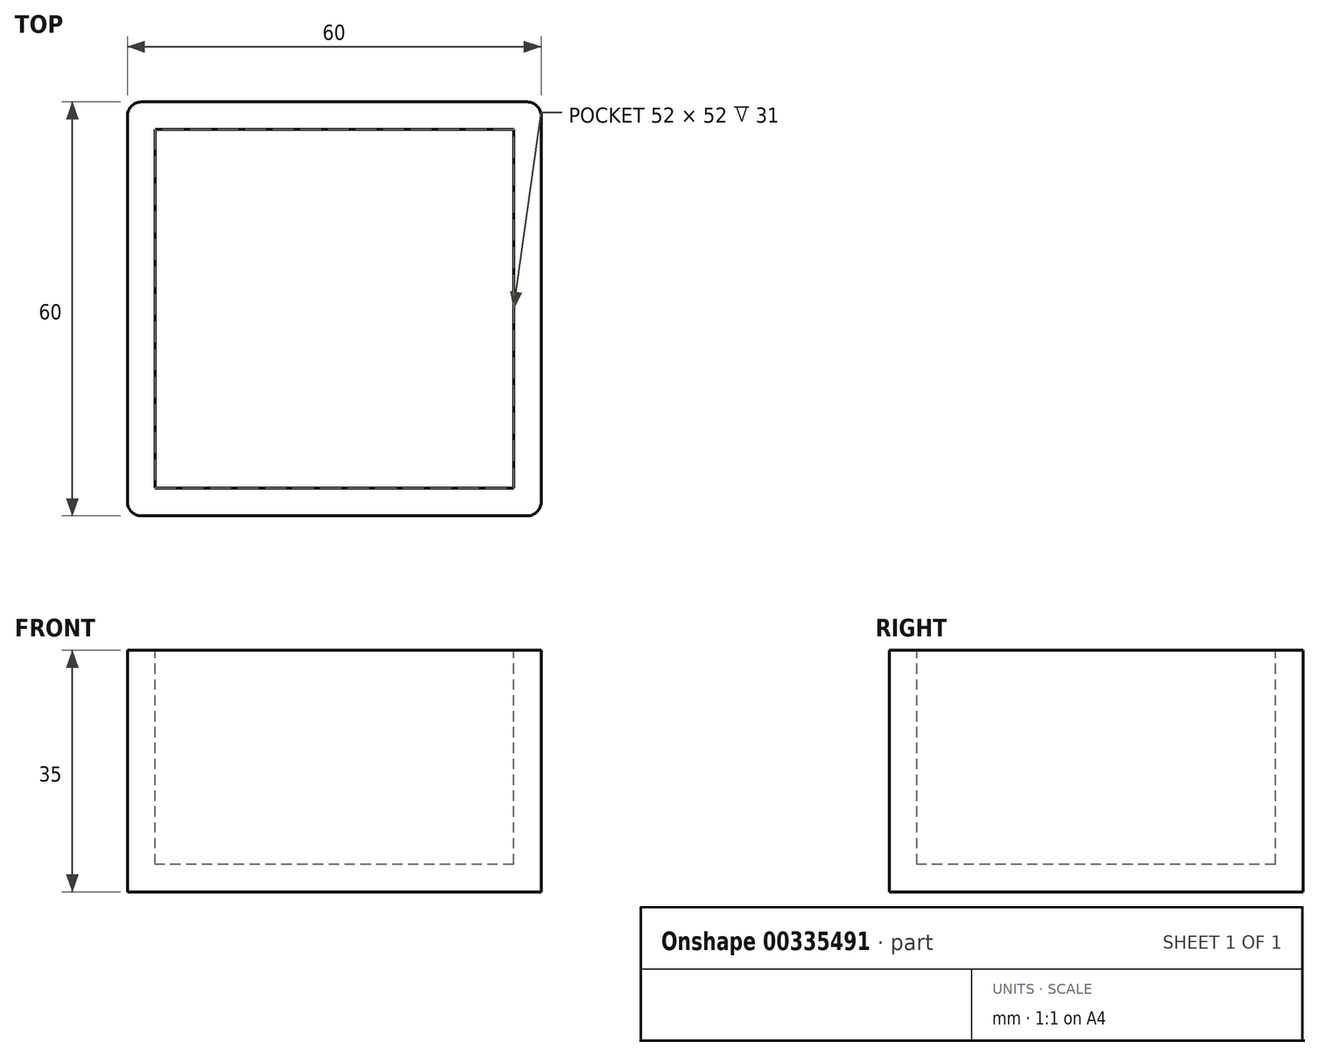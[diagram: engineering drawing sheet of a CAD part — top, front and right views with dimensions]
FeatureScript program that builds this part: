
annotation { "Feature Type Name" : "Feature", "Feature Type Description" : "" }
export const myFeature = defineFeature(function(context is Context, id is Id, definition is map)
    precondition{}
    {
        {
            var Q0;
            Q0=qCreatedBy(makeId("Top.planeOp"),FACE);
            var sketch = newSketch(context, id + "F0", { "sketchPlane" : qUnion([Q0])});
            skLineSegment(sketch, "E0.bottom", {"start": v(-24.12, 22.03) * mm, "end": v(35.88, 22.03) * mm});
            skLineSegment(sketch, "E0.top", {"start": v(-24.12, -37.97) * mm, "end": v(35.88, -37.97) * mm});
            skLineSegment(sketch, "E0.left", {"start": v(-24.12, 22.03) * mm, "end": v(-24.12, -37.97) * mm});
            skLineSegment(sketch, "E0.right", {"start": v(35.88, 22.03) * mm, "end": v(35.88, -37.97) * mm});
            skSolve(sketch);
        }
        {
            var Q0;
            Q0=makeQuery(id+"F0.imprint","IMPRINT",FACE,{"disambiguationData":[TD([[makeQuery(id+"F0.imprint","IMPRINT",EDGE,{"derivedFrom":sQuery(id+"F0.wireOp",EDGE,"E0.bottom")}),-1.0]])]});
            extrude(context, id + "F1", {"entities" : qUnion([Q0]), "depth" : 35 * mm});
        }
        {
            var Q0;
            Q0=makeQuery(id+"F1.opExtrude","CAP_FACE",FACE,{"disambiguationData":[OSD([sQuery(id+"F0.wireOp",EDGE,"E0.bottom"),sQuery(id+"F0.wireOp",EDGE,"E0.top"),sQuery(id+"F0.wireOp",EDGE,"E0.left"),sQuery(id+"F0.wireOp",EDGE,"E0.right")])],"isStart":false});
            var sketch = newSketch(context, id + "F2", { "sketchPlane" : qUnion([Q0])});
            skLineSegment(sketch, "E1.0", {"start": v(-20.12, 18.03) * mm, "end": v(-20.12, -33.97) * mm});
            skLineSegment(sketch, "E1.1", {"start": v(31.88, 18.03) * mm, "end": v(-20.12, 18.03) * mm});
            skLineSegment(sketch, "E1.2", {"start": v(31.88, -33.97) * mm, "end": v(31.88, 18.03) * mm});
            skLineSegment(sketch, "E1.3", {"start": v(-20.12, -33.97) * mm, "end": v(31.88, -33.97) * mm});
            skLineSegment(sketch, "E2.0", {"start": v(-29.12, 27.03) * mm, "end": v(-29.12, -42.97) * mm});
            skLineSegment(sketch, "E2.1", {"start": v(40.88, 27.03) * mm, "end": v(-29.12, 27.03) * mm});
            skLineSegment(sketch, "E2.2", {"start": v(40.88, -42.97) * mm, "end": v(40.88, 27.03) * mm});
            skLineSegment(sketch, "E2.3", {"start": v(-29.12, -42.97) * mm, "end": v(40.88, -42.97) * mm});
            skSolve(sketch);
        }
        {
            var Q0;
            Q0=makeQuery(id+"F2.imprint","IMPRINT",FACE,{"disambiguationData":[TD([[makeQuery(id+"F2.imprint","IMPRINT",EDGE,{"derivedFrom":sQuery(id+"F2.wireOp",EDGE,"E1.0")}),1.0]])]});
            extrude(context, id + "F3", {"entities" : qUnion([Q0]), "operationType" : NewBodyOperationType.REMOVE, "oppositeDirection" : true, "depth" : 31 * mm});
        }
        {
            var Q0;
            Q0=makeQuery(id+"F1.opExtrude","SWEPT_EDGE",EDGE,{"disambiguationData":[OSD([sQuery(id+"F0.wireOp",EDGE,"E0.bottom"),sQuery(id+"F0.wireOp",EDGE,"E0.left")])]});
            var Q1;
            Q1=makeQuery(id+"F1.opExtrude","SWEPT_EDGE",EDGE,{"disambiguationData":[OSD([sQuery(id+"F0.wireOp",EDGE,"E0.bottom"),sQuery(id+"F0.wireOp",EDGE,"E0.right")])]});
            var Q2;
            Q2=makeQuery(id+"F1.opExtrude","SWEPT_EDGE",EDGE,{"disambiguationData":[OSD([sQuery(id+"F0.wireOp",EDGE,"E0.top"),sQuery(id+"F0.wireOp",EDGE,"E0.left")])]});
            var Q3;
            Q3=makeQuery(id+"F1.opExtrude","SWEPT_EDGE",EDGE,{"disambiguationData":[OSD([sQuery(id+"F0.wireOp",EDGE,"E0.top"),sQuery(id+"F0.wireOp",EDGE,"E0.right")])]});
            fillet(context, id + "F4", {"entities" : qUnion([Q0, Q1, Q2, Q3]), "radius" : 2 * mm, "tangentPropagation" : true, "allowEdgeOverflow" : false});
        }
    });
